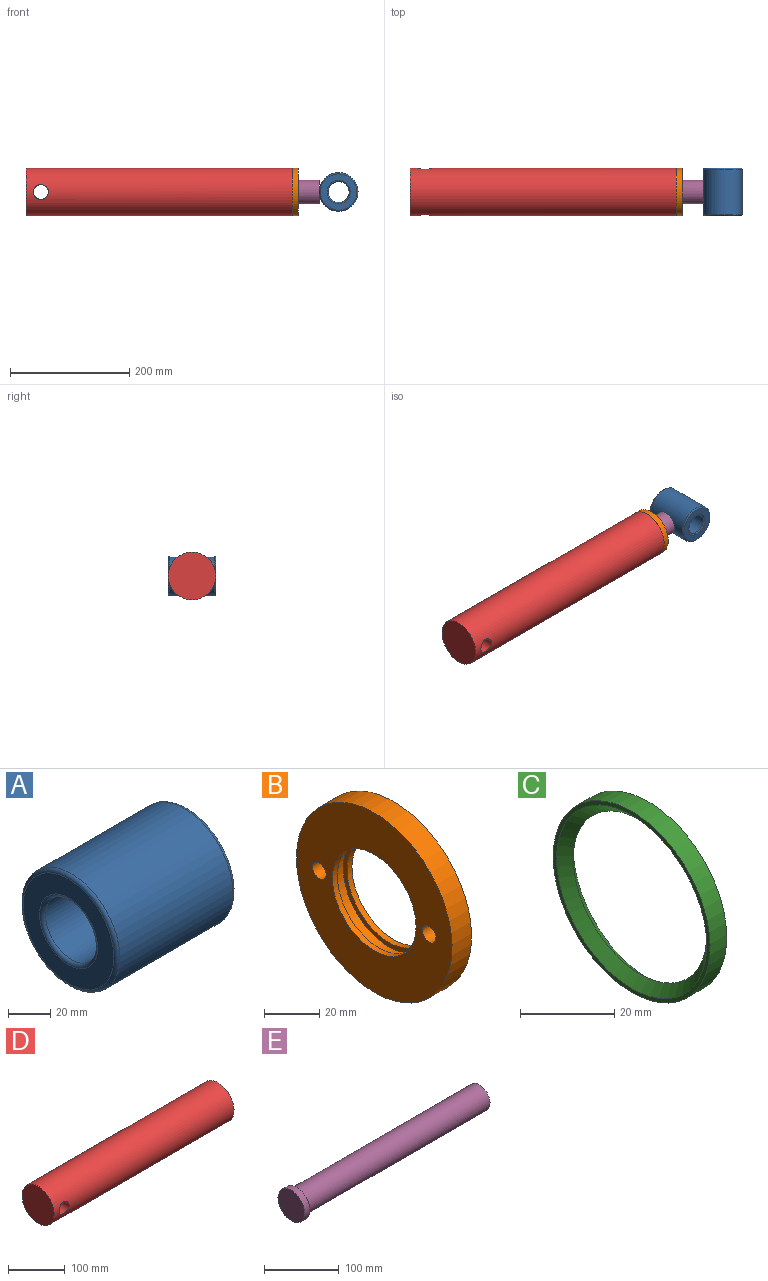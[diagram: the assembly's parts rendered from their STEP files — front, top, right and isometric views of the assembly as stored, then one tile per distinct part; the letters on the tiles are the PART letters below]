
ASSEMBLY  parts=5 mates=4
PART A: 9 faces, bbox 80x70.4x70.4 mm
  f0: cylinder r=17.5mm len=76mm, axis (-1,0,0), area 8299.6mm2, adj f4,f6,f8
  f1: cylinder r=32.5mm len=76mm, axis (-1,0,0), area 15462.6mm2, adj f5,f7,f8
  f2: plane 61x61mm, normal (1,0,0), area 1727.9mm2, adj f6,f7
  f3: plane 61x61mm, normal (-1,0,0), area 1727.9mm2, adj f4,f5
  f4: torus R=19.5mm, axis (1,0,0), area 359.8mm2, adj f0,f3
  f5: torus R=30.5mm, axis (1,0,0), area 627.2mm2, adj f1,f3
  f6: torus R=19.5mm, axis (1,0,0), area 359.8mm2, adj f0,f2
  f7: torus R=30.5mm, axis (1,0,0), area 627.2mm2, adj f1,f2
  f8: cylinder r=4.25mm len=15.52mm, axis (0,-1,0), area 403.8mm2, adj f0,f1
PART B: 12 faces, bbox 10x80x80 mm
  f0: plane 80x80mm, normal (-1,0,0), area 3497.4mm2, adj f1,f3,f8,f10
  f1: cylinder r=21.5mm len=43mm, axis (-1,0,0), area 337.7mm2, adj f0,f7
  f2: cylinder r=21.5mm len=43mm, axis (-1,0,0), area 337.7mm2, adj f4,f6
  f3: cylinder r=40mm len=80mm, axis (-1,0,0), area 2513.3mm2, adj f0,f4
  f4: plane 80x80mm, normal (1,0,0), area 3574.3mm2, adj f2,f3
  f5: cylinder r=23.5mm len=47mm, axis (-1,0,0), area 738.3mm2, adj f6,f7
  f6: plane 47x47mm, normal (-1,0,0), area 282.7mm2, adj f2,f5
  f7: plane 47x47mm, normal (1,0,0), area 282.7mm2, adj f1,f5
  f8: cylinder r=3.5mm len=8mm, axis (-1,0,0), area 175.9mm2, adj f0,f9
  f9: plane 7x7mm, normal (-1,0,0), area 38.5mm2, adj f8
  f10: cylinder r=3.5mm len=8mm, axis (-1,0,0), area 175.9mm2, adj f0,f11
  f11: plane 7x7mm, normal (-1,0,0), area 38.5mm2, adj f10
PART C: 5 faces, bbox 5x47x47 mm
  f0: cylinder r=23.5mm len=47mm, axis (-1,0,0), area 738.3mm2, adj f1,f2
  f1: plane 47x47mm, normal (1,0,0), area 144.5mm2, adj f0,f3
  f2: plane 47x47mm, normal (-1,0,0), area 144.5mm2, adj f0,f4
  f3: cone r=20mm half-angle=45deg, axis (1,0,0), area 472.1mm2, adj f1,f4
  f4: cone r=22.5mm half-angle=45deg, axis (-1,0,0), area 472.1mm2, adj f2,f3
PART D: 6 faces, bbox 447.5x80x80 mm
  f0: cylinder r=40mm len=447.5mm, axis (-1,0,0), area 111475.7mm2, adj f1,f2,f5
  f1: plane 80x80mm, normal (1,0,0), area 1178.1mm2, adj f0,f3
  f2: plane 80x80mm, normal (-1,0,0), area 5026.5mm2, adj f0
  f3: cylinder r=35mm len=407.5mm, axis (1,0,0), area 89613.9mm2, adj f1,f4
  f4: plane 70x70mm, normal (1,0,0), area 3848.5mm2, adj f3
  f5: cylinder r=12.5mm len=80mm, axis (0,-1,0), area 6126.9mm2, adj f0
PART E: 5 faces, bbox 355x50x50 mm
  f0: cylinder r=25mm len=50mm, axis (-1,0,0), area 1570.8mm2, adj f1,f3
  f1: plane 50x50mm, normal (-1,0,0), area 1963.5mm2, adj f0
  f2: cylinder r=20mm len=345mm, axis (1,0,0), area 43354mm2, adj f3,f4
  f3: plane 50x50mm, normal (1,0,0), area 706.9mm2, adj f0,f2
  f4: plane 40x40mm, normal (1,0,0), area 1256.6mm2, adj f2
PLACE A rot(axis=(0,0,1),90deg) t=(-153.48,-69.99,225.85)mm
PLACE B rot(axis=(0,-1,0),180deg) t=(-221.07,-29.99,225.85)mm
PLACE C rot(axis=(0,-1,0),180deg) t=(-223.57,-29.99,225.85)mm
PLACE D t=(-678.57,-29.99,225.85)mm
PLACE E t=(-541.07,-29.99,225.85)mm
MATE fastened B.f3 <-> D.f3  axis (-1,0,0) through (-231.07,-29.99,225.85)mm
MATE fastened A.f8 <-> E.f2  axis (1,0,0) through (-186.07,-29.99,225.85)mm
MATE fastened C.f0 <-> B.f3  axis (1,0,0) through (-226.07,-29.99,225.85)mm
MATE slider E.f0 <-> D.f0  axis (1,0,0) through (-531.07,-29.99,225.85)mm
